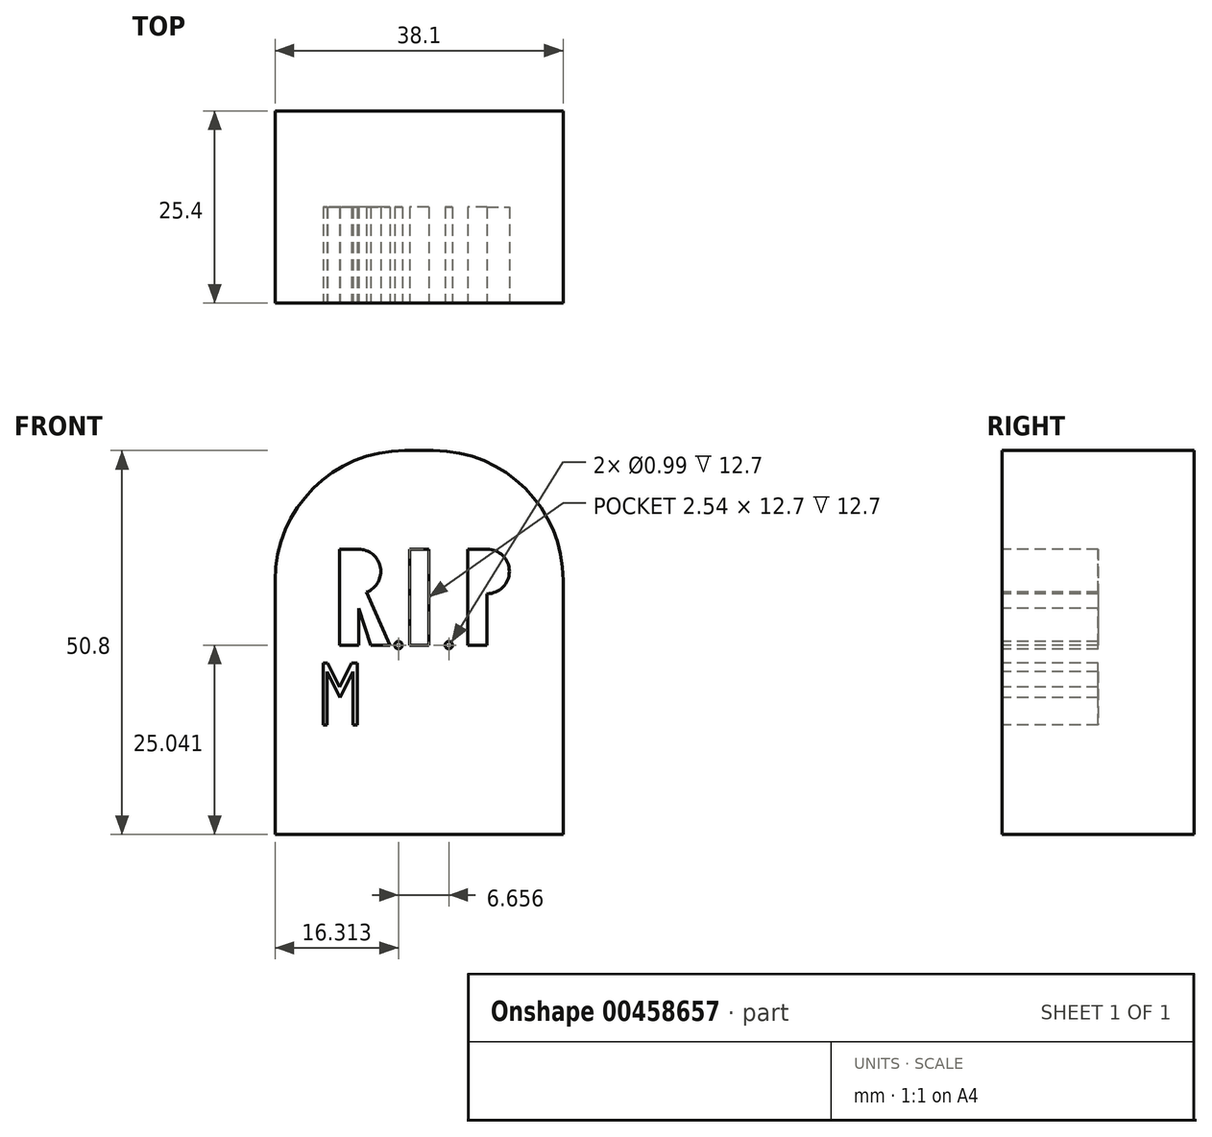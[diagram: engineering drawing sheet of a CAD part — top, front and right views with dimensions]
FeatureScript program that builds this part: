
annotation { "Feature Type Name" : "Feature", "Feature Type Description" : "" }
export const myFeature = defineFeature(function(context is Context, id is Id, definition is map)
    precondition{}
    {
        {
            var Q0;
            Q0=qCreatedBy(makeId("Top.planeOp"),FACE);
            var sketch = newSketch(context, id + "F0", { "sketchPlane" : qUnion([Q0])});
            skLineSegment(sketch, "E0.bottom", {"start": v(-19.05, 12.7) * mm, "end": v(19.05, 12.7) * mm});
            skLineSegment(sketch, "E0.top", {"start": v(-19.05, -12.7) * mm, "end": v(19.05, -12.7) * mm});
            skLineSegment(sketch, "E0.left", {"start": v(-19.05, 12.7) * mm, "end": v(-19.05, -12.7) * mm});
            skLineSegment(sketch, "E0.right", {"start": v(19.05, 12.7) * mm, "end": v(19.05, -12.7) * mm});
            skPoint(sketch, "E0.middle", {"position": v(0, 0) * mm});
            skSolve(sketch);
        }
        {
            var Q0;
            Q0=makeQuery(id+"F0.imprint","IMPRINT",FACE,{"disambiguationData":[TD([[makeQuery(id+"F0.imprint","IMPRINT",EDGE,{"derivedFrom":sQuery(id+"F0.wireOp",EDGE,"E0.bottom")}),-1.0]])]});
            extrude(context, id + "F1", {"entities" : qUnion([Q0]), "depth" : 50.8 * mm});
        }
        {
            var Q0;
            Q0=makeQuery(id+"F1.opExtrude","CAP_EDGE",EDGE,{"disambiguationData":[OSD([sQuery(id+"F0.wireOp",EDGE,"E0.right")])],"isStart":false});
            var Q1;
            Q1=makeQuery(id+"F1.opExtrude","CAP_EDGE",EDGE,{"disambiguationData":[OSD([sQuery(id+"F0.wireOp",EDGE,"E0.left")])],"isStart":false});
            fillet(context, id + "F2", {"entities" : qUnion([Q0, Q1]), "radius" : 17.17 * mm, "tangentPropagation" : true, "allowEdgeOverflow" : false});
        }
        {
            var Q0;
            Q0=makeQuery(id+"F1.opExtrude","SWEPT_FACE",FACE,{"disambiguationData":[OSD([sQuery(id+"F0.wireOp",EDGE,"E0.top")])]});
            var sketch = newSketch(context, id + "F3", { "sketchPlane" : qUnion([Q0])});
            skLineSegment(sketch, "E1", {"start": v(1.27, 37.74) * mm, "end": v(-1.27, 37.74) * mm});
            skLineSegment(sketch, "E2", {"start": v(-1.27, 37.74) * mm, "end": v(-1.27, 25.04) * mm});
            skLineSegment(sketch, "E3", {"start": v(1.27, 37.74) * mm, "end": v(1.27, 25.04) * mm});
            skLineSegment(sketch, "E4", {"start": v(1.27, 25.04) * mm, "end": v(0, 25.04) * mm});
            skLineSegment(sketch, "E5", {"start": v(0, 25.04) * mm, "end": v(-1.27, 25.04) * mm});
            skSolve(sketch);
        }
        {
            var Q0;
            Q0 = qSketchRegion(id + "F3", true);
            extrude(context, id + "F4", {"entities" : qUnion([Q0]), "operationType" : NewBodyOperationType.REMOVE, "oppositeDirection" : true, "depth" : 12.7 * mm});
        }
        {
            var Q0;
            Q0=makeQuery(id+"F1.opExtrude","SWEPT_FACE",FACE,{"disambiguationData":[OSD([sQuery(id+"F0.wireOp",EDGE,"E0.top")])]});
            var sketch = newSketch(context, id + "F5", { "sketchPlane" : qUnion([Q0])});
            skLineSegment(sketch, "E6", {"start": v(1.27, 25.04) * mm, "end": v(6.35, 25.04) * mm});
            skLineSegment(sketch, "E7", {"start": v(-1.27, 25.04) * mm, "end": v(-13.97, 25.04) * mm});
            skSolve(sketch);
        }
        {
            var Q0;
            {var subQ0=sQuery(id+"F0.wireOp",EDGE,"E0.top");Q0=makeQuery(id+"F5.imprint","IMPRINT",FACE,{"disambiguationData":[TD([[makeQuery(id+"F5.imprint","IMPRINT",EDGE,{"derivedFrom":makeQuery(id+"F1.opExtrude","CAP_EDGE",EDGE,{"disambiguationData":[OSD([subQ0])],"isStart":true})}),1.0]])]});}
            var sketch = newSketch(context, id + "F6", { "sketchPlane" : qUnion([Q0])});
            skLineSegment(sketch, "E8", {"start": v(6.44, 25.04) * mm, "end": v(6.44, 37.74) * mm});
            skLineSegment(sketch, "E9", {"start": v(6.44, 37.74) * mm, "end": v(8.98, 37.74) * mm});
            skLineSegment(sketch, "E10", {"start": v(8.98, 37.74) * mm, "end": v(8.98, 25.04) * mm});
            skLineSegment(sketch, "E11", {"start": v(8.98, 25.04) * mm, "end": v(6.44, 25.04) * mm});
            skArc(sketch, "E12", {"start": v(8.98, 37.74) * mm, "mid": v(11.92, 34.8) * mm, "end": v(8.98, 31.85) * mm});
            skSolve(sketch);
        }
        {
            var Q0;
            Q0 = qSketchRegion(id + "F6", true);
            extrude(context, id + "F7", {"entities" : qUnion([Q0]), "operationType" : NewBodyOperationType.REMOVE, "oppositeDirection" : true, "depth" : 12.7 * mm});
        }
        {
            var Q0;
            {var subQ0=sQuery(id+"F0.wireOp",EDGE,"E0.top");Q0=makeQuery(id+"F5.imprint","IMPRINT",FACE,{"disambiguationData":[TD([[makeQuery(id+"F5.imprint","IMPRINT",EDGE,{"derivedFrom":makeQuery(id+"F1.opExtrude","CAP_EDGE",EDGE,{"disambiguationData":[OSD([subQ0])],"isStart":true})}),1.0]])]});}
            var sketch = newSketch(context, id + "F8", { "sketchPlane" : qUnion([Q0])});
            skLineSegment(sketch, "E13", {"start": v(-10.56, 25.04) * mm, "end": v(-8.02, 25.04) * mm});
            skLineSegment(sketch, "E14", {"start": v(-8.02, 25.04) * mm, "end": v(-8.02, 37.74) * mm});
            skLineSegment(sketch, "E15", {"start": v(-8.02, 37.74) * mm, "end": v(-10.56, 37.74) * mm});
            skLineSegment(sketch, "E16", {"start": v(-10.56, 37.74) * mm, "end": v(-10.56, 25.04) * mm});
            skArc(sketch, "E17", {"start": v(-8.02, 37.74) * mm, "mid": v(-5.08, 34.8) * mm, "end": v(-8.02, 31.85) * mm});
            skLineSegment(sketch, "E18", {"start": v(-6.95, 32.05) * mm, "end": v(-3.88, 25.04) * mm});
            skLineSegment(sketch, "E19", {"start": v(-3.88, 25.04) * mm, "end": v(-6.42, 25.04) * mm});
            skLineSegment(sketch, "E20", {"start": v(-6.42, 25.04) * mm, "end": v(-8.02, 29.9) * mm});
            skSolve(sketch);
        }
        {
            var Q0;
            Q0 = qSketchRegion(id + "F8", true);
            extrude(context, id + "F9", {"entities" : qUnion([Q0]), "operationType" : NewBodyOperationType.REMOVE, "oppositeDirection" : true, "depth" : 12.7 * mm});
        }
        {
            var Q0;
            {var subQ0=sQuery(id+"F0.wireOp",EDGE,"E0.top");Q0=makeQuery(id+"F5.imprint","IMPRINT",FACE,{"disambiguationData":[TD([[makeQuery(id+"F5.imprint","IMPRINT",EDGE,{"derivedFrom":makeQuery(id+"F1.opExtrude","CAP_EDGE",EDGE,{"disambiguationData":[OSD([subQ0])],"isStart":true})}),1.0]])]});}
            var sketch = newSketch(context, id + "F10", { "sketchPlane" : qUnion([Q0])});
            skCircle(sketch, "E21", {"center": v(-2.74, 25.04) * mm, "radius": 0.5 * mm});
            skCircle(sketch, "E22", {"center": v(3.92, 25.04) * mm, "radius": 0.5 * mm});
            skSolve(sketch);
        }
        {
            var Q0;
            Q0 = qSketchRegion(id + "F10", true);
            extrude(context, id + "F11", {"entities" : qUnion([Q0]), "operationType" : NewBodyOperationType.REMOVE, "oppositeDirection" : true, "depth" : 12.7 * mm});
        }
        {
            var Q0;
            {var subQ0=sQuery(id+"F0.wireOp",EDGE,"E0.top");Q0=makeQuery(id+"F5.imprint","IMPRINT",FACE,{"disambiguationData":[TD([[makeQuery(id+"F5.imprint","IMPRINT",EDGE,{"derivedFrom":makeQuery(id+"F1.opExtrude","CAP_EDGE",EDGE,{"disambiguationData":[OSD([subQ0])],"isStart":true})}),1.0]])]});}
            var sketch = newSketch(context, id + "F12", { "sketchPlane" : qUnion([Q0])});
            skLineSegment(sketch, "E23", {"start": v(-12.77, 14.47) * mm, "end": v(9.83, 14.47) * mm});
            skSolve(sketch);
        }
        {
            var Q0;
            {var subQ0=sQuery(id+"F0.wireOp",EDGE,"E0.top");Q0=makeQuery(id+"F5.imprint","IMPRINT",FACE,{"disambiguationData":[TD([[makeQuery(id+"F5.imprint","IMPRINT",EDGE,{"derivedFrom":makeQuery(id+"F1.opExtrude","CAP_EDGE",EDGE,{"disambiguationData":[OSD([subQ0])],"isStart":true})}),1.0]])]});}
            var sketch = newSketch(context, id + "F13", { "sketchPlane" : qUnion([Q0])});
            skLineSegment(sketch, "E24", {"start": v(-12.69, 14.47) * mm, "end": v(-12.69, 22.7) * mm});
            skLineSegment(sketch, "E25", {"start": v(-12.69, 22.7) * mm, "end": v(-12.14, 22.7) * mm});
            skLineSegment(sketch, "E26", {"start": v(-12.14, 22.7) * mm, "end": v(-10.54, 19.5) * mm});
            skLineSegment(sketch, "E27", {"start": v(-10.54, 19.5) * mm, "end": v(-8.95, 22.7) * mm});
            skLineSegment(sketch, "E28", {"start": v(-8.95, 22.7) * mm, "end": v(-8.2, 22.7) * mm});
            skLineSegment(sketch, "E29", {"start": v(-8.2, 22.7) * mm, "end": v(-8.2, 14.47) * mm});
            skLineSegment(sketch, "E30", {"start": v(-8.2, 14.47) * mm, "end": v(-8.72, 14.47) * mm});
            skLineSegment(sketch, "E31", {"start": v(-8.72, 14.47) * mm, "end": v(-8.72, 21.56) * mm});
            skLineSegment(sketch, "E32", {"start": v(-8.72, 21.56) * mm, "end": v(-10.44, 18.1) * mm});
            skLineSegment(sketch, "E33", {"start": v(-10.44, 18.1) * mm, "end": v(-12.16, 21.56) * mm});
            skLineSegment(sketch, "E34", {"start": v(-12.16, 21.56) * mm, "end": v(-12.16, 14.47) * mm});
            skLineSegment(sketch, "E35", {"start": v(-12.16, 14.47) * mm, "end": v(-12.69, 14.47) * mm});
            skSolve(sketch);
        }
        {
            var Q0;
            Q0 = qSketchRegion(id + "F13", true);
            extrude(context, id + "F14", {"entities" : qUnion([Q0]), "operationType" : NewBodyOperationType.REMOVE, "oppositeDirection" : true, "depth" : 12.7 * mm});
        }
    });
